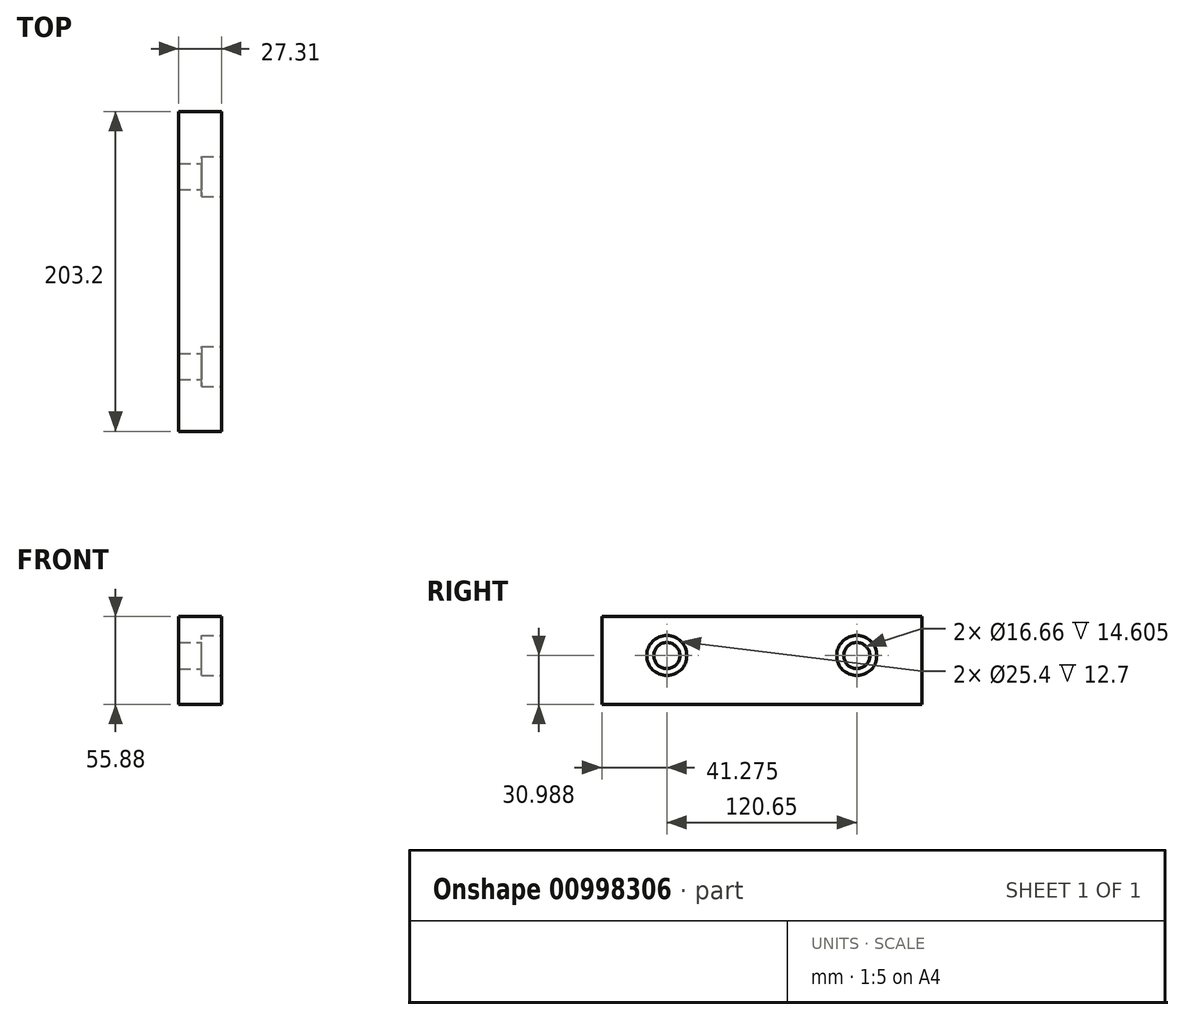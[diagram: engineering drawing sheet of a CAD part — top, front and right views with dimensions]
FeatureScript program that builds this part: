
annotation { "Feature Type Name" : "Feature", "Feature Type Description" : "" }
export const myFeature = defineFeature(function(context is Context, id is Id, definition is map)
    precondition{}
    {
        {
            var Q0;
            Q0=qCreatedBy(makeId("Front.planeOp"),FACE);
            var sketch = newSketch(context, id + "F0", { "sketchPlane" : qUnion([Q0])});
            skLineSegment(sketch, "E0.bottom", {"start": v(0, 0) * mm, "end": v(27.3, 0) * mm});
            skLineSegment(sketch, "E0.top", {"start": v(0, 55.88) * mm, "end": v(27.3, 55.88) * mm});
            skLineSegment(sketch, "E0.left", {"start": v(0, 0) * mm, "end": v(0, 55.88) * mm});
            skLineSegment(sketch, "E0.right", {"start": v(27.3, 0) * mm, "end": v(27.3, 55.88) * mm});
            skSolve(sketch);
        }
        {
            var Q0;
            Q0=makeQuery(id+"F0.imprint","IMPRINT",FACE,{"disambiguationData":[TD([[makeQuery(id+"F0.imprint","IMPRINT",EDGE,{"derivedFrom":sQuery(id+"F0.wireOp",EDGE,"E0.bottom")}),1.0]])]});
            extrude(context, id + "F1", {"entities" : qUnion([Q0]), "endBound" : BoundingType.SYMMETRIC, "depth" : 203.2 * mm, "offsetDistance" : 25.4 * mm});
        }
        {
            var Q0;
            Q0=makeQuery(id+"F1.opExtrude","SWEPT_FACE",FACE,{"disambiguationData":[OSD([sQuery(id+"F0.wireOp",EDGE,"E0.right")])]});
            var sketch = newSketch(context, id + "F2", { "sketchPlane" : qUnion([Q0])});
            skCircle(sketch, "E1", {"center": v(-60.33, 30.99) * mm, "radius": 8.33 * mm});
            skLineSegment(sketch, "E2", {"start": v(0, 0) * mm, "end": v(0, 55.88) * mm, "construction": true});
            skCircle(sketch, "E3", {"center": v(60.33, 30.99) * mm, "radius": 8.33 * mm});
            skSolve(sketch);
        }
        {
            var Q0;
            Q0 = qSketchRegion(id + "F2", true);
            extrude(context, id + "F3", {"entities" : qUnion([Q0]), "operationType" : NewBodyOperationType.REMOVE, "oppositeDirection" : true, "depth" : 38.1 * mm, "offsetDistance" : 25.4 * mm});
        }
        {
            var Q0;
            Q0=makeQuery(id+"F1.opExtrude","SWEPT_FACE",FACE,{"disambiguationData":[OSD([sQuery(id+"F0.wireOp",EDGE,"E0.right")])]});
            var sketch = newSketch(context, id + "F4", { "sketchPlane" : qUnion([Q0])});
            skCircle(sketch, "E4", {"center": v(-60.33, 30.99) * mm, "radius": 12.7 * mm});
            skCircle(sketch, "E5", {"center": v(60.33, 30.99) * mm, "radius": 12.7 * mm});
            skSolve(sketch);
        }
        {
            var Q0;
            Q0=makeQuery(id+"F4.imprint","IMPRINT",FACE,{"disambiguationData":[TD([[makeQuery(id+"F4.imprint","IMPRINT",EDGE,{"derivedFrom":sQuery(id+"F4.wireOp",EDGE,"E4")}),1.0]])]});
            var Q1;
            Q1=makeQuery(id+"F4.imprint","IMPRINT",FACE,{"disambiguationData":[TD([[makeQuery(id+"F4.imprint","IMPRINT",EDGE,{"derivedFrom":sQuery(id+"F4.wireOp",EDGE,"E5")}),1.0]])]});
            extrude(context, id + "F5", {"entities" : qUnion([Q0, Q1]), "operationType" : NewBodyOperationType.REMOVE, "oppositeDirection" : true, "depth" : 12.7 * mm, "offsetDistance" : 25.4 * mm});
        }
    });
